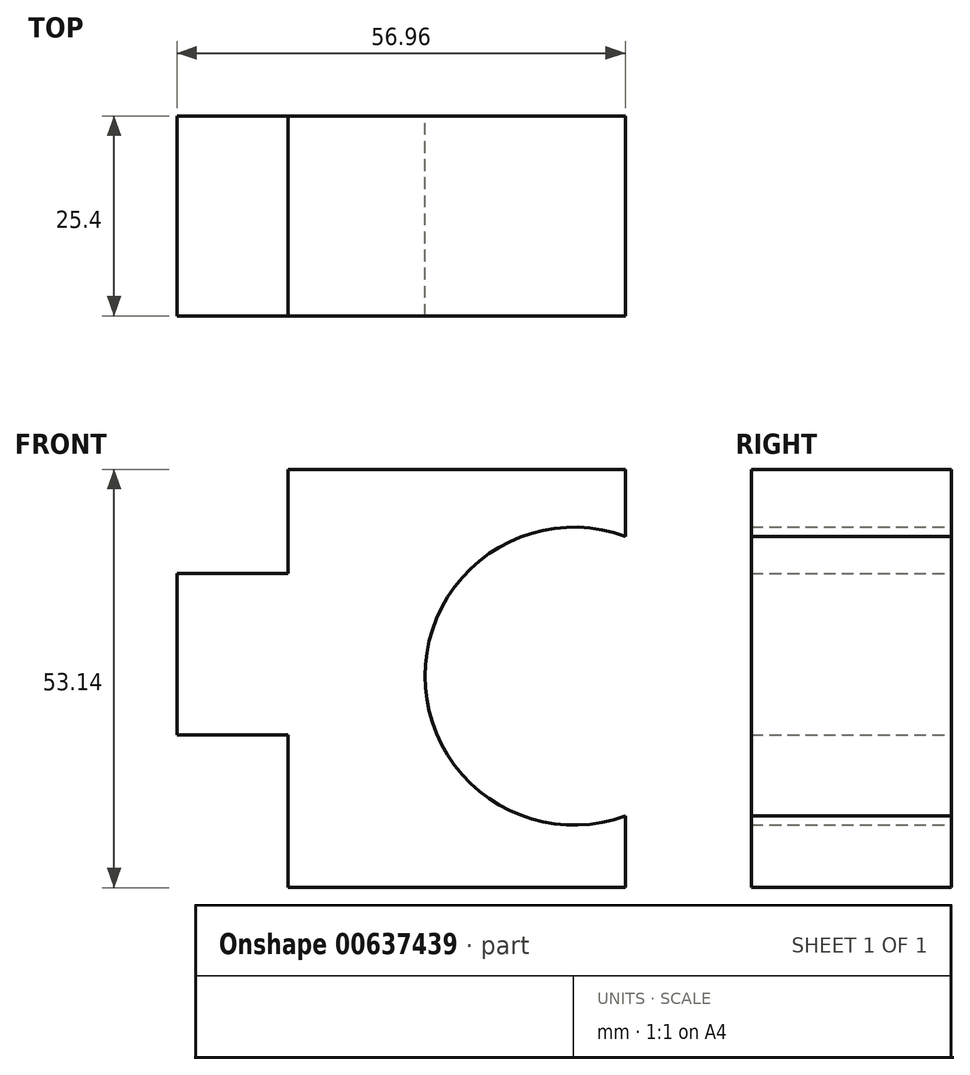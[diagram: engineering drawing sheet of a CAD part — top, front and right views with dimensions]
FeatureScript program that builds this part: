
annotation { "Feature Type Name" : "Feature", "Feature Type Description" : "" }
export const myFeature = defineFeature(function(context is Context, id is Id, definition is map)
    precondition{}
    {
        {
            var Q0;
            Q0=qCreatedBy(makeId("Front.planeOp"),FACE);
            var sketch = newSketch(context, id + "F0", { "sketchPlane" : qUnion([Q0])});
            skLineSegment(sketch, "E0", {"start": v(-23.93, -30.83) * mm, "end": v(18.94, -30.83) * mm});
            skLineSegment(sketch, "E1", {"start": v(18.94, -30.83) * mm, "end": v(18.94, -21.73) * mm});
            skLineSegment(sketch, "E2", {"start": v(-23.93, -30.83) * mm, "end": v(-23.93, -11.45) * mm});
            skLineSegment(sketch, "E3", {"start": v(-23.93, -11.45) * mm, "end": v(-38.02, -11.45) * mm});
            skLineSegment(sketch, "E4", {"start": v(-38.02, -11.45) * mm, "end": v(-38.02, 9.1) * mm});
            skLineSegment(sketch, "E5", {"start": v(-38.02, 9.1) * mm, "end": v(-23.93, 9.1) * mm});
            skLineSegment(sketch, "E6", {"start": v(-23.93, 9.1) * mm, "end": v(-23.93, 22.31) * mm});
            skLineSegment(sketch, "E7", {"start": v(-23.93, 22.31) * mm, "end": v(18.94, 22.31) * mm});
            skLineSegment(sketch, "E8", {"start": v(18.94, 22.31) * mm, "end": v(18.94, 13.8) * mm});
            skArc(sketch, "E9", {"start": v(18.94, 13.8) * mm, "mid": v(-6.5, -3.96) * mm, "end": v(18.94, -21.73) * mm});
            skSolve(sketch);
        }
        {
            var Q0;
            Q0 = qSketchRegion(id + "F0", true);
            extrude(context, id + "F1", {"entities" : qUnion([Q0]), "depth" : 25.4 * mm, "offsetDistance" : 25.4 * mm});
        }
    });
